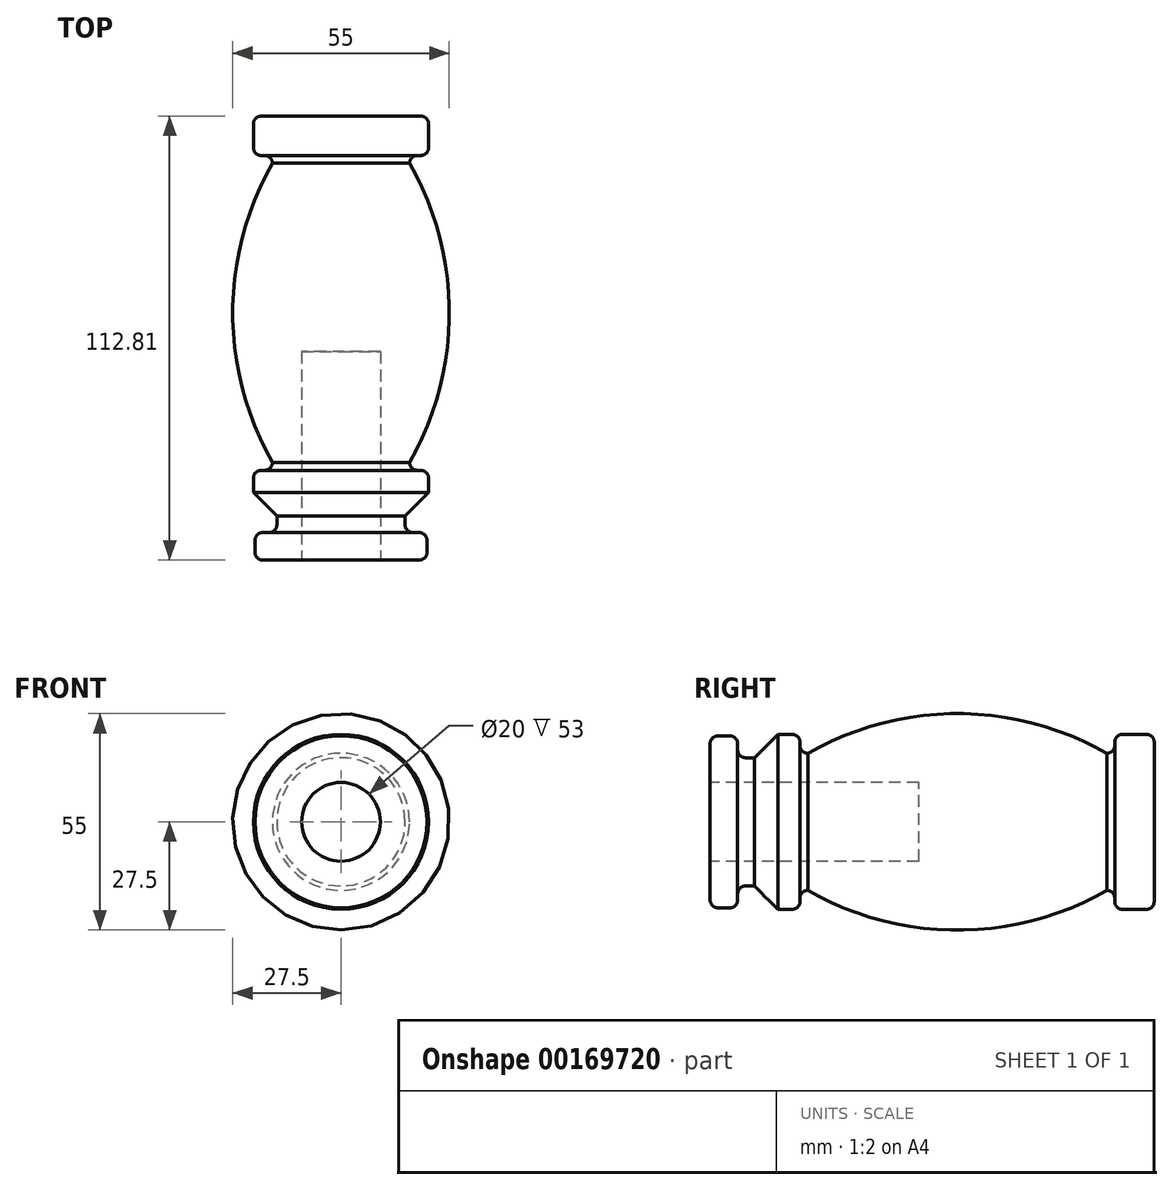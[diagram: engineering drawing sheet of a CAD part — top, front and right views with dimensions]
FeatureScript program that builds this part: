
annotation { "Feature Type Name" : "Feature", "Feature Type Description" : "" }
export const myFeature = defineFeature(function(context is Context, id is Id, definition is map)
    precondition{}
    {
        {
            var Q0;
            Q0=qCreatedBy(makeId("Right.planeOp"),FACE);
            var sketch = newSketch(context, id + "F0", { "sketchPlane" : qUnion([Q0])});
            skLineSegment(sketch, "E0", {"start": v(-45.97, 10) * mm, "end": v(-45.97, 19.86) * mm});
            skLineSegment(sketch, "E1", {"start": v(-43.97, 21.86) * mm, "end": v(-40.97, 21.86) * mm});
            skLineSegment(sketch, "E2", {"start": v(-38.97, 19.86) * mm, "end": v(-38.97, 18.3) * mm});
            skLineSegment(sketch, "E3", {"start": v(-36.97, 16.3) * mm, "end": v(-34.7, 16.3) * mm});
            skLineSegment(sketch, "E4", {"start": v(-34.7, 16.3) * mm, "end": v(-28.75, 22.25) * mm});
            skLineSegment(sketch, "E5", {"start": v(66.84, 20.25) * mm, "end": v(66.84, 0) * mm});
            skLineSegment(sketch, "E6", {"start": v(-28.75, 22.25) * mm, "end": v(-25.16, 22.25) * mm});
            skLineSegment(sketch, "E7", {"start": v(-23.16, 20.25) * mm, "end": v(-23.16, 19.41) * mm});
            skLineSegment(sketch, "E8", {"start": v(56.84, 19.41) * mm, "end": v(56.84, 20.25) * mm});
            skLineSegment(sketch, "E9", {"start": v(58.84, 22.25) * mm, "end": v(64.84, 22.25) * mm});
            skLineSegment(sketch, "E10", {"start": v(-45.97, 10) * mm, "end": v(7.03, 10) * mm});
            skLineSegment(sketch, "E11", {"start": v(7.03, 10) * mm, "end": v(7.03, 0) * mm});
            skPoint(sketch, "E12.orphan", {"position": v(-45.97, 0) * mm});
            skLineSegment(sketch, "E13", {"start": v(7.03, 0) * mm, "end": v(66.84, 0) * mm});
            skPoint(sketch, "E14.visualSharp", {"position": v(-45.97, 21.86) * mm});
            skArc(sketch, "E14.filletArc", {"start": v(-43.97, 21.86) * mm, "mid": v(-45.39, 21.27) * mm, "end": v(-45.97, 19.86) * mm});
            skPoint(sketch, "E15.visualSharp", {"position": v(-38.97, 21.86) * mm});
            skArc(sketch, "E15.filletArc", {"start": v(-38.97, 19.86) * mm, "mid": v(-39.56, 21.27) * mm, "end": v(-40.97, 21.86) * mm});
            skPoint(sketch, "E16.visualSharp", {"position": v(-23.16, 17.41) * mm});
            skArc(sketch, "E16.filletArc", {"start": v(-23.16, 19.41) * mm, "mid": v(-22.57, 18) * mm, "end": v(-21.16, 17.41) * mm});
            skPoint(sketch, "E17.visualSharp", {"position": v(56.84, 17.41) * mm});
            skArc(sketch, "E17.filletArc", {"start": v(54.84, 17.41) * mm, "mid": v(56.25, 18) * mm, "end": v(56.84, 19.41) * mm});
            skPoint(sketch, "E18.visualSharp", {"position": v(56.84, 22.25) * mm});
            skArc(sketch, "E18.filletArc", {"start": v(58.84, 22.25) * mm, "mid": v(57.43, 21.67) * mm, "end": v(56.84, 20.25) * mm});
            skPoint(sketch, "E19.visualSharp", {"position": v(66.84, 22.25) * mm});
            skArc(sketch, "E19.filletArc", {"start": v(66.84, 20.25) * mm, "mid": v(66.25, 21.67) * mm, "end": v(64.84, 22.25) * mm});
            skPoint(sketch, "E20.visualSharp", {"position": v(-23.16, 22.25) * mm});
            skArc(sketch, "E20.filletArc", {"start": v(-23.16, 20.25) * mm, "mid": v(-23.75, 21.67) * mm, "end": v(-25.16, 22.25) * mm});
            skPoint(sketch, "E21.visualSharp", {"position": v(-38.97, 16.3) * mm});
            skArc(sketch, "E21.filletArc", {"start": v(-38.97, 18.3) * mm, "mid": v(-38.39, 16.88) * mm, "end": v(-36.97, 16.3) * mm});
            skLineSegment(sketch, "E22", {"start": v(-45.97, 0) * mm, "end": v(115.35, 0) * mm, "construction": true});
            skArc(sketch, "E23", {"start": v(54.84, 17.41) * mm, "mid": v(16.84, 27.5) * mm, "end": v(-21.16, 17.41) * mm});
            skSolve(sketch);
        }
        {
            var Q0;
            Q0=qSketchRegion(id+"F0",true);
            var Q1;
            Q1=sQuery(id+"F0.wireOp",EDGE,"E22");
            revolve(context, id + "F1", {"entities" : qUnion([Q0]), "axis" : qUnion([Q1]), "revolveType" : RevolveType.FULL});
        }
    });
